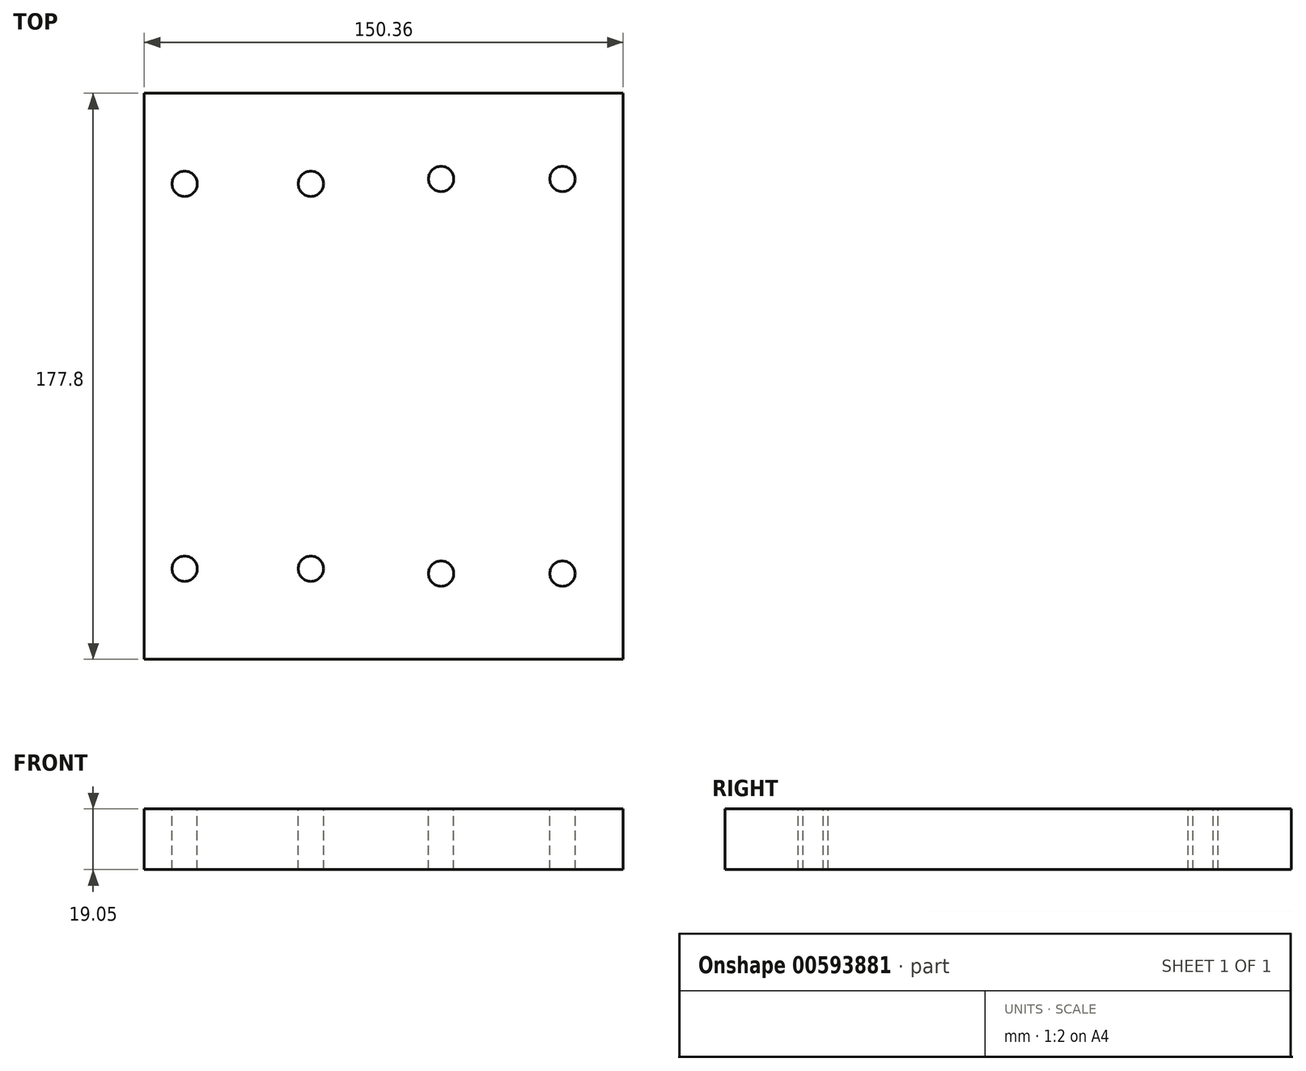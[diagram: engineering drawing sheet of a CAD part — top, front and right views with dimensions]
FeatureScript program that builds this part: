
annotation { "Feature Type Name" : "Feature", "Feature Type Description" : "" }
export const myFeature = defineFeature(function(context is Context, id is Id, definition is map)
    precondition{}
    {
        {
            var Q0;
            Q0=qCreatedBy(makeId("Top.planeOp"),FACE);
            var sketch = newSketch(context, id + "F0", { "sketchPlane" : qUnion([Q0])});
            skLineSegment(sketch, "E0.bottom", {"start": v(-75.18, 88.9) * mm, "end": v(75.18, 88.9) * mm});
            skLineSegment(sketch, "E0.top", {"start": v(-75.18, -88.9) * mm, "end": v(75.18, -88.9) * mm});
            skLineSegment(sketch, "E0.left", {"start": v(-75.18, 88.9) * mm, "end": v(-75.18, -88.9) * mm});
            skLineSegment(sketch, "E0.right", {"start": v(75.18, 88.9) * mm, "end": v(75.18, -88.9) * mm});
            skPoint(sketch, "E0.middle", {"position": v(0, 0) * mm});
            skSolve(sketch);
        }
        {
            var Q0;
            Q0 = qSketchRegion(id + "F0", true);
            extrude(context, id + "F1", {"entities" : qUnion([Q0]), "depth" : 19.05 * mm, "offsetDistance" : 25.4 * mm});
        }
        {
            var Q0;
            Q0=makeQuery(id+"F1.opExtrude","CAP_FACE",FACE,{"disambiguationData":[OSD([sQuery(id+"F0.wireOp",EDGE,"E0.bottom"),sQuery(id+"F0.wireOp",EDGE,"E0.top"),sQuery(id+"F0.wireOp",EDGE,"E0.left"),sQuery(id+"F0.wireOp",EDGE,"E0.right")])],"isStart":false});
            var sketch = newSketch(context, id + "F2", { "sketchPlane" : qUnion([Q0])});
            skLineSegment(sketch, "E1", {"start": v(75.18, 0) * mm, "end": v(-75.18, 0) * mm, "construction": true});
            skLineSegment(sketch, "E2.0", {"start": v(56.13, 88.9) * mm, "end": v(56.13, -88.9) * mm, "construction": true});
            skLineSegment(sketch, "E3.0", {"start": v(18.03, 88.9) * mm, "end": v(18.03, -88.9) * mm, "construction": true});
            skLineSegment(sketch, "E4.0", {"start": v(75.18, 61.98) * mm, "end": v(18.03, 61.98) * mm, "construction": true});
            skLineSegment(sketch, "E5.MirrorCS", {"start": v(75.18, -61.98) * mm, "end": v(18.03, -61.98) * mm, "construction": true});
            skPoint(sketch, "E6.orphan", {"position": v(-75.18, 61.98) * mm});
            skPoint(sketch, "E7.orphan", {"position": v(-75.18, -61.98) * mm});
            skPoint(sketch, "E8", {"position": v(18.03, 61.98) * mm});
            skPoint(sketch, "E9", {"position": v(56.13, 61.98) * mm});
            skPoint(sketch, "E10", {"position": v(56.13, -61.98) * mm});
            skPoint(sketch, "E11", {"position": v(18.03, -61.98) * mm});
            skLineSegment(sketch, "E12.0", {"start": v(-62.48, 88.9) * mm, "end": v(-62.48, -88.9) * mm, "construction": true});
            skLineSegment(sketch, "E13.0", {"start": v(-22.86, 88.9) * mm, "end": v(-22.86, -88.9) * mm, "construction": true});
            skLineSegment(sketch, "E14.0", {"start": v(75.18, 60.45) * mm, "end": v(-75.18, 60.45) * mm, "construction": true});
            skPoint(sketch, "E15", {"position": v(-62.48, 60.45) * mm});
            skPoint(sketch, "E16", {"position": v(-22.86, 60.45) * mm});
            skPoint(sketch, "E17.MirrorP", {"position": v(-62.48, -60.45) * mm});
            skPoint(sketch, "E18.MirrorP", {"position": v(-22.86, -60.45) * mm});
            skSolve(sketch);
        }
        {
            var Q0;
            Q0=sQuery(id+"F2.wireOp",VERTEX,"E8");
            var Q1;
            Q1=sQuery(id+"F2.wireOp",VERTEX,"E9");
            var Q2;
            Q2=sQuery(id+"F2.wireOp",VERTEX,"E11");
            var Q3;
            Q3=sQuery(id+"F2.wireOp",VERTEX,"E10");
            var Q4;
            Q4=sQuery(id+"F2.wireOp",VERTEX,"E15");
            var Q5;
            Q5=sQuery(id+"F2.wireOp",VERTEX,"E16");
            var Q6;
            Q6=sQuery(id+"F2.wireOp",VERTEX,"E17.MirrorP");
            var Q7;
            Q7=sQuery(id+"F2.wireOp",VERTEX,"E18.MirrorP");
            var Q8;
            Q8=makeQuery(id+"F1.opExtrude","SWEPT_BODY",BODY,{"disambiguationData":[OSD([sQuery(id+"F0.wireOp",EDGE,"E0.bottom"),sQuery(id+"F0.wireOp",EDGE,"E0.top"),sQuery(id+"F0.wireOp",EDGE,"E0.left"),sQuery(id+"F0.wireOp",EDGE,"E0.right")])]});
            hole(context, id + "F3", {"style" : HoleStyle.SIMPLE, "endStyle" : HoleEndStyle.THROUGH, "standardTappedOrClearance" : lookupTablePath({ "standard" : "ANSI", "engagement" : "75%", "pitch" : "16 tpi", "size" : "3/8", "type" : "Tapped" }), "standardBlindInLast" : lookupTablePath({ "standard" : "ANSI", "engagement" : "75%", "pitch" : "16 tpi", "size" : "3/8", "type" : "Tapped" }), "holeDiameter" : 7.94 * mm, "majorDiameter" : 9.52 * mm, "showTappedDepth" : true, "isTappedThrough" : true, "tappedDepth" : 25.4 * mm, "tapClearance" : 3, "locations" : qUnion([Q0, Q1, Q2, Q3, Q4, Q5, Q6, Q7]), "scope" : qUnion([Q8])});
        }
    });
